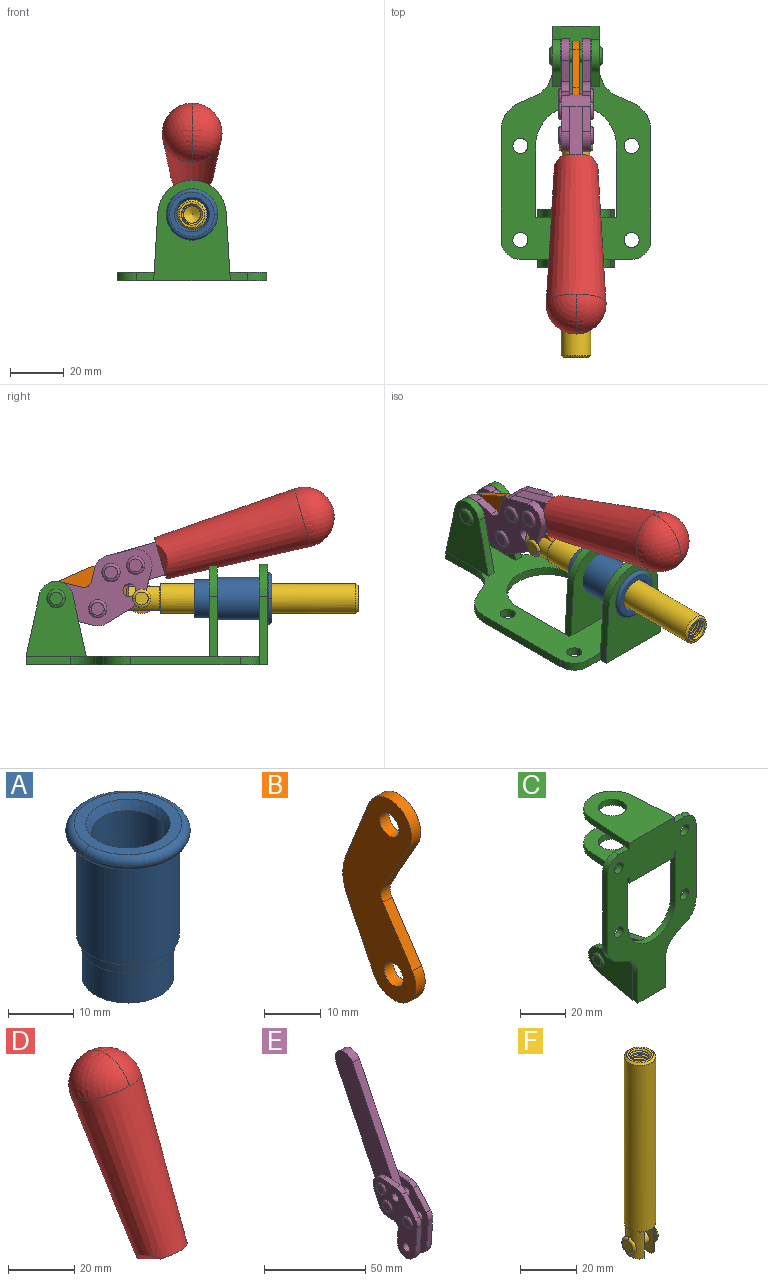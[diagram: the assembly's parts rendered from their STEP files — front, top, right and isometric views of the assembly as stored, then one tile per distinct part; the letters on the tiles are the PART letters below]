
ASSEMBLY  parts=6 mates=6
PART A: 15 faces, bbox 20.6x20.6x28.7 mm
  f0: torus R=8.26mm, axis (0,0,1), area 56.8mm2, adj f1,f10,f12
  f1: torus R=8.26mm, axis (0,0,1), area 56.8mm2, adj f0,f6,f13
  f2: cylinder r=5.59mm len=25.91mm, axis (0,0,1), area 909.6mm2, adj f3,f4
  f3: cone r=6.86mm half-angle=45deg, axis (0,0,-1), area 70.2mm2, adj f2,f14
  f4: cone r=6.47mm half-angle=30deg, axis (0,0,1), area 66.7mm2, adj f2,f13
  f5: cylinder r=7.04mm len=14.07mm, axis (0,0,1), area 252.6mm2, adj f11,f14
  f6: torus R=8.26mm, axis (0,0,1), area 56.8mm2, adj f1,f12,f13
  f7: cylinder r=7.16mm len=14.33mm, axis (0,0,1), area 91.5mm2, adj f9,f11
  f8: cylinder r=7.86mm len=18.42mm, axis (0,0,1), area 909.6mm2, adj f9,f10
  f9: plane 15.72x15.72mm, normal (0,0,-1), area 33mm2, adj f7,f8
  f10: plane 16.51x16.51mm, normal (0,0,-1), area 19.9mm2, adj f0,f8,f12
  f11: plane 14.33x14.33mm, normal (0,0,-1), area 5.7mm2, adj f5,f7
  f12: torus R=8.26mm, axis (0,0,1), area 56.8mm2, adj f0,f6,f10
  f13: plane 16.51x16.51mm, normal (0,0,1), area 82.7mm2, adj f1,f4,f6
  f14: plane 14.07x14.07mm, normal (0,0,-1), area 7.8mm2, adj f3,f5
PART B: 12 faces, bbox 2.3x18.2x42.8 mm
  f0: cylinder r=2.4mm len=4.8mm, axis (1,0,0), area 34.9mm2, adj f4,f11
  f1: cylinder r=10.41mm len=8.47mm, axis (1,0,0), area 20.2mm2, adj f4,f9,f10,f11
  f2: cylinder r=3.05mm len=3.16mm, axis (1,0,0), area 7.7mm2, adj f4,f6,f7,f11
  f3: cylinder r=2.4mm len=4.8mm, axis (1,0,0), area 34.9mm2, adj f4,f11
  f4: plane 42.81x18.23mm, normal (-1,0,0), area 414.1mm2, adj f0,f1,f2,f3,f5,f6,f7,f8
  f5: cylinder r=5.54mm len=10.67mm, axis (1,0,0), area 41.8mm2, adj f4,f6,f10,f11
  f6: plane 11.66x6.53mm, normal (0,-0.87,-0.49), area 30.9mm2, adj f2,f4,f5,f11
  f7: plane 11.17x7.33mm, normal (0,-0.84,0.55), area 30.9mm2, adj f2,f4,f8,f11
  f8: cylinder r=5.54mm len=10.51mm, axis (1,0,0), area 41.8mm2, adj f4,f7,f9,f11
  f9: plane 13.67x6.67mm, normal (0,0.9,-0.44), area 35.1mm2, adj f1,f4,f8,f11
  f10: plane 14.1x5.7mm, normal (0,0.93,0.37), area 35.1mm2, adj f1,f4,f5,f11
  f11: plane 42.81x18.23mm, normal (1,0,0), area 414.1mm2, adj f0,f1,f2,f3,f5,f6,f7,f8
PART C: 55 faces, bbox 55.7x37.4x89.8 mm
  f0: torus R=2.41mm, axis (-1,0,0), area 15mm2, adj f11,f15,f25
  f1: torus R=2.41mm, axis (-1,0,0), area 15mm2, adj f10,f12,f22
  f2: cylinder r=2.78mm len=5.56mm, axis (0,-1,0), area 54.2mm2, adj f30,f54
  f3: cylinder r=14.99mm len=29.97mm, axis (0,-1,0), area 145.9mm2, adj f30,f49,f53,f54
  f4: cylinder r=2.78mm len=5.56mm, axis (0,-1,0), area 54.2mm2, adj f30,f54
  f5: cylinder r=2.78mm len=5.56mm, axis (0,-1,0), area 54.2mm2, adj f30,f54
  f6: cylinder r=2.78mm len=5.56mm, axis (0,-1,0), area 54.2mm2, adj f30,f54
  f7: cylinder r=6.35mm len=12.7mm, axis (0,0,1), area 123.6mm2, adj f27,f51
  f8: cylinder r=6.35mm len=12.7mm, axis (0,0,-1), area 124.7mm2, adj f21,f35
  f9: cylinder r=2.41mm len=11.18mm, axis (-1,0,0), area 169.4mm2, adj f16,f19
  f10: plane 4.83x4.83mm, normal (1,0,0), area 18.3mm2, adj f1,f12
  f11: plane 4.83x4.83mm, normal (-1,0,0), area 18.3mm2, adj f0,f15
  f12: torus R=2.41mm, axis (-1,0,0), area 15mm2, adj f1,f10,f22
  f13: cylinder r=6.35mm len=12.41mm, axis (1,0,0), area 53.4mm2, adj f18,f19,f22,f23
  f14: cylinder r=6.35mm len=12.41mm, axis (-1,0,0), area 53.4mm2, adj f16,f17,f24,f25
  f15: torus R=2.41mm, axis (-1,0,0), area 15mm2, adj f0,f11,f25
  f16: plane 27.86x22.35mm, normal (1,0,0), area 425.4mm2, adj f9,f14,f17,f24,f30
  f17: plane 22.86x4.97mm, normal (0,0.21,0.98), area 72.5mm2, adj f14,f16,f25,f30
  f18: plane 22.86x4.97mm, normal (0,0.21,0.98), area 72.5mm2, adj f13,f19,f22,f30
  f19: plane 27.86x22.35mm, normal (-1,0,0), area 425.4mm2, adj f9,f13,f18,f23,f30
  f20: cylinder r=12.7mm len=25.35mm, axis (0,0,-1), area 119.8mm2, adj f21,f34,f35,f36
  f21: plane 34.21x28.07mm, normal (0,0,-1), area 702.4mm2, adj f8,f20,f30,f34,f36
  f22: plane 27.96x22.45mm, normal (1,0,0), area 407.2mm2, adj f1,f12,f13,f18,f23,f30,f42,f43
  f23: plane 22.86x4.97mm, normal (0,0.21,-0.98), area 72.5mm2, adj f13,f19,f22,f44
  f24: plane 22.86x4.97mm, normal (0,0.21,-0.98), area 72.5mm2, adj f14,f16,f25,f44
  f25: plane 27.86x22.35mm, normal (-1,0,0), area 407.1mm2, adj f0,f14,f15,f17,f24,f30,f45,f46
  f26: plane 3.1x0.95mm, normal (0,0,-1), area 2.7mm2, adj f30,f49,f50,f54
  f27: plane 34.21x28.07mm, normal (0,0,1), area 702.4mm2, adj f7,f28,f30,f50,f52
  f28: cylinder r=12.7mm len=25.35mm, axis (0,0,1), area 118.8mm2, adj f27,f50,f51,f52
  f29: plane 3.1x0.95mm, normal (0,0,-1), area 2.7mm2, adj f30,f52,f53,f54
  f30: plane 86.54x55.63mm, normal (0,1,0), area 2362.9mm2, adj f2,f3,f4,f5,f6,f16,f17,f18
  f31: plane 40.56x3.1mm, normal (-1,0,0), area 125.7mm2, adj f30,f32,f48,f54
  f32: cylinder r=7.11mm len=7.11mm, axis (0,-1,0), area 34.6mm2, adj f30,f31,f33,f54
  f33: plane 6.67x3.1mm, normal (0,0,1), area 20.4mm2, adj f30,f32,f34,f54
  f34: plane 25.39x3.13mm, normal (-1,0.06,0), area 79.5mm2, adj f20,f21,f33,f35,f54
  f35: plane 37.31x28.45mm, normal (0,0,1), area 789.9mm2, adj f8,f20,f34,f36,f54
  f36: plane 25.39x3.13mm, normal (1,0.06,0), area 79.5mm2, adj f20,f21,f35,f37,f54
  f37: plane 6.67x3.1mm, normal (0,0,1), area 20.4mm2, adj f30,f36,f38,f54
  f38: cylinder r=7.11mm len=7.11mm, axis (0,-1,0), area 34.6mm2, adj f30,f37,f39,f54
  f39: plane 40.56x3.1mm, normal (1,0,0), area 125.7mm2, adj f30,f38,f40,f54
  f40: cylinder r=11.18mm len=10.16mm, axis (0,-1,0), area 39.5mm2, adj f30,f39,f41,f54
  f41: plane 6.09x3.1mm, normal (0.42,0,-0.91), area 20.8mm2, adj f30,f40,f42,f54
  f42: cylinder r=11.18mm len=9.41mm, axis (0,-1,0), area 37.2mm2, adj f22,f30,f41,f43,f54
  f43: plane 16.5x3.1mm, normal (1,0,0), area 51.1mm2, adj f22,f42,f44,f54
  f44: plane 17.37x3.1mm, normal (0,0,-1), area 53.8mm2, adj f23,f24,f30,f43,f45,f54
  f45: plane 16.5x3.1mm, normal (-1,0,0), area 51.1mm2, adj f25,f44,f46,f54
  f46: cylinder r=11.18mm len=9.41mm, axis (0,-1,0), area 37.2mm2, adj f25,f30,f45,f47,f54
  f47: plane 6.09x3.1mm, normal (-0.42,0,-0.91), area 20.8mm2, adj f30,f46,f48,f54
  f48: cylinder r=11.18mm len=10.16mm, axis (0,-1,0), area 39.5mm2, adj f30,f31,f47,f54
  f49: plane 26.54x3.1mm, normal (-1,0,0), area 82.3mm2, adj f3,f26,f30,f54
  f50: plane 25.39x3.1mm, normal (1,0.06,0), area 78.8mm2, adj f26,f27,f28,f51,f54
  f51: plane 37.31x28.45mm, normal (0,0,-1), area 789.9mm2, adj f7,f28,f50,f52,f54
  f52: plane 25.39x3.1mm, normal (-1,0.06,0), area 78.8mm2, adj f27,f28,f29,f51,f54
  f53: plane 26.54x3.1mm, normal (1,0,0), area 82.3mm2, adj f3,f29,f30,f54
  f54: plane 89.66x55.63mm, normal (0,-1,0), area 2678.5mm2, adj f2,f3,f4,f5,f6,f26,f29,f31
PART D: 11 faces, bbox 22.3x42.6x64.5 mm
  f0: sphere r=11.13mm, area 411.4mm2, adj f1,f8
  f1: cone r=11.11mm half-angle=3.3deg, axis (0,0.44,0.9), area 3251.8mm2, adj f0,f7,f8,f9,f10
  f2: cylinder r=6.16mm len=11.7mm, axis (1,0,0), area 89.5mm2, adj f3,f4,f5,f6
  f3: plane 60.23x36.75mm, normal (-1,0,0), area 763.6mm2, adj f2,f4,f6,f10
  f4: plane 51.37x25.05mm, normal (0,0.9,-0.44), area 264.2mm2, adj f2,f3,f5,f10
  f5: plane 60.23x36.75mm, normal (1,0,0), area 763.6mm2, adj f2,f4,f6,f10
  f6: plane 51.37x25.05mm, normal (0,-0.9,0.44), area 264.2mm2, adj f2,f3,f5,f10
  f7: plane 9.95x5.95mm, normal (0.71,-0.31,-0.64), area 25.8mm2, adj f1,f10
  f8: sphere r=11.13mm, area 411.4mm2, adj f0,f1
  f9: plane 9.95x5.95mm, normal (-0.71,-0.31,-0.64), area 25.8mm2, adj f1,f10
  f10: plane 14.27x11.38mm, normal (0,-0.44,-0.9), area 106.7mm2, adj f1,f3,f4,f5,f6,f7,f9
PART E: 59 faces, bbox 12.9x60.2x99.6 mm
  f0: torus R=2.39mm, axis (-1,0,0), area 14.9mm2, adj f20,f43,f51
  f1: torus R=2.39mm, axis (-1,0,0), area 14.9mm2, adj f19,f42,f51
  f2: torus R=2.39mm, axis (-1,0,0), area 14.9mm2, adj f18,f35,f51
  f3: torus R=2.39mm, axis (-1,0,0), area 14.9mm2, adj f14,f17,f23
  f4: torus R=2.39mm, axis (-1,0,0), area 14.9mm2, adj f13,f16,f23
  f5: torus R=2.39mm, axis (-1,0,0), area 14.9mm2, adj f12,f15,f23
  f6: cylinder r=2.39mm len=4.78mm, axis (1,0,0), area 46.5mm2, adj f48,f50,f51
  f7: cylinder r=2.39mm len=4.78mm, axis (1,0,0), area 46.5mm2, adj f50,f51
  f8: cylinder r=6.35mm len=12.68mm, axis (1,0,0), area 61.8mm2, adj f38,f39,f50,f51
  f9: cylinder r=2.39mm len=4.78mm, axis (-1,0,0), area 70.5mm2, adj f46,f50
  f10: cylinder r=2.39mm len=4.78mm, axis (-1,0,0), area 46.5mm2, adj f23,f45,f46
  f11: cylinder r=2.39mm len=4.78mm, axis (-1,0,0), area 46.5mm2, adj f23,f46
  f12: plane 4.78x4.78mm, normal (1,0,0), area 17.9mm2, adj f5,f15
  f13: plane 4.78x4.78mm, normal (1,0,0), area 17.9mm2, adj f4,f16
  f14: plane 4.78x4.78mm, normal (1,0,0), area 17.9mm2, adj f3,f17
  f15: torus R=2.39mm, axis (-1,0,0), area 14.9mm2, adj f5,f12,f23
  f16: torus R=2.39mm, axis (-1,0,0), area 14.9mm2, adj f4,f13,f23
  f17: torus R=2.39mm, axis (-1,0,0), area 14.9mm2, adj f3,f14,f23
  f18: plane 4.78x4.78mm, normal (-1,0,0), area 17.9mm2, adj f2,f35
  f19: plane 4.78x4.78mm, normal (-1,0,0), area 17.9mm2, adj f1,f42
  f20: plane 4.78x4.78mm, normal (-1,0,0), area 17.9mm2, adj f0,f43
  f21: plane 2.26x0.2mm, normal (1,0,0), area 0.2mm2, adj f31,f44
  f22: plane 2.26x0.2mm, normal (-1,0,0), area 0.2mm2, adj f41,f44
  f23: plane 39.37x30.77mm, normal (1,0,0), area 565.5mm2, adj f3,f4,f5,f10,f11,f15,f16,f17
  f24: cylinder r=6.1mm len=4.15mm, axis (-1,0,0), area 14.7mm2, adj f23,f25,f32,f46
  f25: plane 10.25x9.01mm, normal (0,-0.75,0.66), area 42.3mm2, adj f23,f24,f26,f46
  f26: cylinder r=6.35mm len=4.64mm, axis (-1,0,0), area 15.6mm2, adj f23,f25,f27,f46
  f27: plane 15.84x3.1mm, normal (0,-1,-0.07), area 49.2mm2, adj f23,f26,f28,f46
  f28: cylinder r=6.35mm len=12.68mm, axis (-1,0,0), area 61.8mm2, adj f23,f27,f29,f46
  f29: plane 8.11x3.1mm, normal (0,1,0.07), area 25.2mm2, adj f23,f28,f30,f46
  f30: cylinder r=3.05mm len=3.25mm, axis (-1,0,0), area 14.8mm2, adj f23,f29,f31,f46
  f31: plane 5.99x3.1mm, normal (0,0.07,-1), area 18.6mm2, adj f21,f23,f30,f44,f46
  f32: plane 9.5x3.1mm, normal (0,-0.07,1), area 29.5mm2, adj f23,f24,f33,f46,f47
  f33: cylinder r=6.1mm len=8.63mm, axis (-1,0,0), area 39.1mm2, adj f23,f32,f34,f47
  f34: plane 8.65x3.96mm, normal (0,0.91,-0.42), area 29.5mm2, adj f23,f33,f44,f47
  f35: torus R=2.39mm, axis (-1,0,0), area 14.9mm2, adj f2,f18,f51
  f36: plane 10.25x9.01mm, normal (0,-0.75,0.66), area 42.3mm2, adj f37,f49,f50,f51
  f37: cylinder r=6.35mm len=4.64mm, axis (1,0,0), area 15.6mm2, adj f36,f38,f50,f51
  f38: plane 15.84x3.1mm, normal (0,-1,-0.07), area 49.2mm2, adj f8,f37,f50,f51
  f39: plane 8.11x3.1mm, normal (0,1,0.07), area 25.2mm2, adj f8,f40,f50,f51
  f40: cylinder r=3.05mm len=3.25mm, axis (1,0,0), area 14.8mm2, adj f39,f41,f50,f51
  f41: plane 5.99x3.1mm, normal (0,0.07,-1), area 18.6mm2, adj f22,f40,f44,f50,f51
  f42: torus R=2.39mm, axis (-1,0,0), area 14.9mm2, adj f1,f19,f51
  f43: torus R=2.39mm, axis (-1,0,0), area 14.9mm2, adj f0,f20,f51
  f44: cylinder r=6.35mm len=12.12mm, axis (-1,0,0), area 128.9mm2, adj f21,f22,f23,f31,f34,f41,f46,f47
  f45: plane 2.65x1.35mm, normal (1,0,0), area 1mm2, adj f10,f55
  f46: plane 39.08x20.42mm, normal (-1,0,0), area 412.5mm2, adj f9,f10,f11,f24,f25,f26,f27,f28
  f47: plane 77.62x39.82mm, normal (1,0,0), area 850mm2, adj f32,f33,f34,f44,f53,f54,f55
  f48: plane 2.65x1.35mm, normal (-1,0,0), area 1mm2, adj f6,f55
  f49: cylinder r=6.1mm len=4.15mm, axis (1,0,0), area 14.7mm2, adj f36,f50,f51,f56
  f50: plane 39.08x20.42mm, normal (1,0,0), area 412.5mm2, adj f6,f7,f8,f9,f36,f37,f38,f39
  f51: plane 39.37x30.77mm, normal (-1,0,0), area 565.5mm2, adj f0,f1,f2,f6,f7,f8,f35,f36
  f52: plane 8.65x3.96mm, normal (0,0.91,-0.42), area 29.5mm2, adj f44,f51,f57,f58
  f53: plane 68.49x33.4mm, normal (0,0.9,-0.44), area 358.1mm2, adj f44,f47,f54,f58
  f54: cylinder r=6.35mm len=12.06mm, axis (1,0,0), area 93.7mm2, adj f47,f53,f55,f58
  f55: plane 68.49x33.4mm, normal (0,-0.9,0.44), area 358.1mm2, adj f44,f45,f46,f47,f48,f50,f54,f58
  f56: plane 9.5x3.1mm, normal (0,-0.07,1), area 29.5mm2, adj f49,f50,f51,f57,f58
  f57: cylinder r=6.1mm len=8.63mm, axis (1,0,0), area 39.1mm2, adj f51,f52,f56,f58
  f58: plane 77.62x39.82mm, normal (-1,0,0), area 850mm2, adj f44,f52,f53,f54,f55,f56,f57
PART F: 48 faces, bbox 12.6x11.1x86.1 mm
  f0: torus R=2.41mm, axis (-1,0,0), area 15mm2, adj f30,f32,f34
  f1: torus R=2.41mm, axis (-1,0,0), area 15mm2, adj f29,f31,f33
  f2: cylinder r=5.54mm len=72.39mm, axis (0,0,1), area 2518.5mm2, adj f3,f4,f42,f43
  f3: cone r=5.54mm half-angle=45deg, axis (0,0,1), area 7.6mm2, adj f2,f5,f41
  f4: cone r=5.54mm half-angle=45deg, axis (0,0,-1), area 34.9mm2, adj f2,f39
  f5: cylinder r=5.08mm len=11.48mm, axis (0,0,1), area 108.3mm2, adj f3,f7,f8,f41
  f6: cylinder r=2.41mm len=4.83mm, axis (-1,0,0), area 71.2mm2, adj f40,f41
  f7: cylinder r=2.41mm len=4.83mm, axis (-1,0,0), area 7.6mm2, adj f5,f34
  f8: cone r=5.08mm half-angle=45deg, axis (0,0,1), area 10.6mm2, adj f5,f37,f41
  f9: cone r=3.98mm half-angle=45deg, axis (0,0,1), area 17.6mm2, adj f27,f39,f45,f46,f47
  f10: cylinder r=2.41mm len=4.83mm, axis (-1,0,0), area 7.6mm2, adj f33,f38
  f11: cylinder r=3.2mm len=6.4mm, axis (0,0,1), area 78.4mm2, adj f12,f28,f44,f45,f47
  f12: cylinder r=3.2mm len=6.4mm, axis (0,0,1), area 10.5mm2, adj f11,f13,f45,f47
  f13: cylinder r=3.2mm len=6.4mm, axis (0,0,1), area 10.5mm2, adj f12,f14,f45,f47
  f14: cylinder r=3.2mm len=6.4mm, axis (0,0,1), area 10.5mm2, adj f13,f15,f45,f47
  f15: cylinder r=3.2mm len=6.4mm, axis (0,0,1), area 10.5mm2, adj f14,f16,f45,f47
  f16: cylinder r=3.2mm len=6.4mm, axis (0,0,1), area 10.5mm2, adj f15,f17,f45,f47
  f17: cylinder r=3.2mm len=6.4mm, axis (0,0,1), area 10.5mm2, adj f16,f18,f45,f47
  f18: cylinder r=3.2mm len=6.4mm, axis (0,0,1), area 10.5mm2, adj f17,f19,f45,f47
  f19: cylinder r=3.2mm len=6.4mm, axis (0,0,1), area 10.5mm2, adj f18,f20,f45,f47
  f20: cylinder r=3.2mm len=6.4mm, axis (0,0,1), area 10.5mm2, adj f19,f21,f45,f47
  f21: cylinder r=3.2mm len=6.4mm, axis (0,0,1), area 10.5mm2, adj f20,f22,f45,f47
  f22: cylinder r=3.2mm len=6.4mm, axis (0,0,1), area 10.5mm2, adj f21,f23,f45,f47
  f23: cylinder r=3.2mm len=6.4mm, axis (0,0,1), area 10.5mm2, adj f22,f24,f45,f47
  f24: cylinder r=3.2mm len=6.4mm, axis (0,0,1), area 10.5mm2, adj f23,f25,f45,f47
  f25: cylinder r=3.2mm len=6.4mm, axis (0,0,1), area 10.5mm2, adj f24,f26,f45,f47
  f26: cylinder r=3.2mm len=6.4mm, axis (0,0,1), area 10.5mm2, adj f25,f27,f45,f47
  f27: cylinder r=3.2mm len=6.4mm, axis (0,0,1), area 7.4mm2, adj f9,f26,f45,f47
  f28: cone r=3.2mm half-angle=60deg, axis (0,0,1), area 37.2mm2, adj f11
  f29: plane 4.83x4.83mm, normal (-1,0,0), area 18.3mm2, adj f1,f31
  f30: plane 4.83x4.83mm, normal (1,0,0), area 18.3mm2, adj f0,f32
  f31: torus R=2.41mm, axis (-1,0,0), area 15mm2, adj f1,f29,f33
  f32: torus R=2.41mm, axis (-1,0,0), area 15mm2, adj f0,f30,f34
  f33: plane 6.83x6.83mm, normal (1,0,0), area 18.3mm2, adj f1,f10,f31
  f34: plane 6.83x6.83mm, normal (-1,0,0), area 18.3mm2, adj f0,f7,f32
  f35: cone r=5.08mm half-angle=45deg, axis (0,0,1), area 10.6mm2, adj f36,f38,f40
  f36: plane 7.25x1.97mm, normal (0,0,-1), area 10mm2, adj f35,f40
  f37: plane 7.25x1.97mm, normal (0,0,-1), area 10mm2, adj f8,f41
  f38: cylinder r=5.08mm len=11.48mm, axis (0,0,1), area 108.3mm2, adj f10,f35,f40,f42
  f39: plane 9.55x9.55mm, normal (0,0,1), area 22mm2, adj f4,f9
  f40: plane 12.76x10.09mm, normal (1,0,0), area 95.7mm2, adj f6,f35,f36,f38,f42,f43
  f41: plane 12.76x10.09mm, normal (-1,0,0), area 95.7mm2, adj f3,f5,f6,f8,f37,f43
  f42: cone r=5.54mm half-angle=45deg, axis (0,0,1), area 7.6mm2, adj f2,f38,f40
  f43: plane 11.07x4.7mm, normal (0,0,-1), area 50.4mm2, adj f2,f40,f41
  f44: plane 0.89x0.62mm, normal (-1,0,0), area 0.3mm2, adj f11,f45,f46,f47
  f45: bspline ~24.8x7.63mm, area 266.6mm2, adj f9,f11,f12,f13,f14,f15,f16,f17
  f46: bspline ~24.87x7.63mm, area 73.6mm2, adj f9,f44,f45,f47
  f47: bspline ~24.98x7.63mm, area 272.5mm2, adj f9,f11,f12,f13,f14,f15,f16,f17
PLACE A rot(axis=(1,0,0),90deg) t=(0,10.16,0)mm
PLACE B rot(axis=(1,0,0),92deg) t=(0,25.81,0.55)mm
PLACE C rot(axis=(1,0,0),90deg) t=(0,9.14,0)mm fixed
PLACE D rot(axis=(1,0,0),100deg) t=(0.04,13.9,-5.2)mm
PLACE E rot(axis=(1,0,0),100deg) t=(0,13.9,-5.2)mm
PLACE F rot(axis=(1,0,0),90deg) t=(0,24.96,0)mm
MATE slider F.f2 <-> A.f2  axis (0,-1,0) through (0,-33.82,24.61)mm
MATE fastened A.f2 <-> C.f7  axis (0,-1,0) through (0,-37.25,24.61)mm
MATE revolute B.f3 <-> C.f0  axis (1,0,0) through (0,41.23,24.61)mm
MATE fastened D.f2 <-> E.f54  axis (-1,0,0) through (2.35,-52.38,55.25)mm
MATE revolute E.f7 <-> C.f0  axis (-1,0,0) through (0,41.23,24.61)mm
MATE revolute B.f5 <-> F.f6  axis (1,0,0) through (0,9.48,24.61)mm
